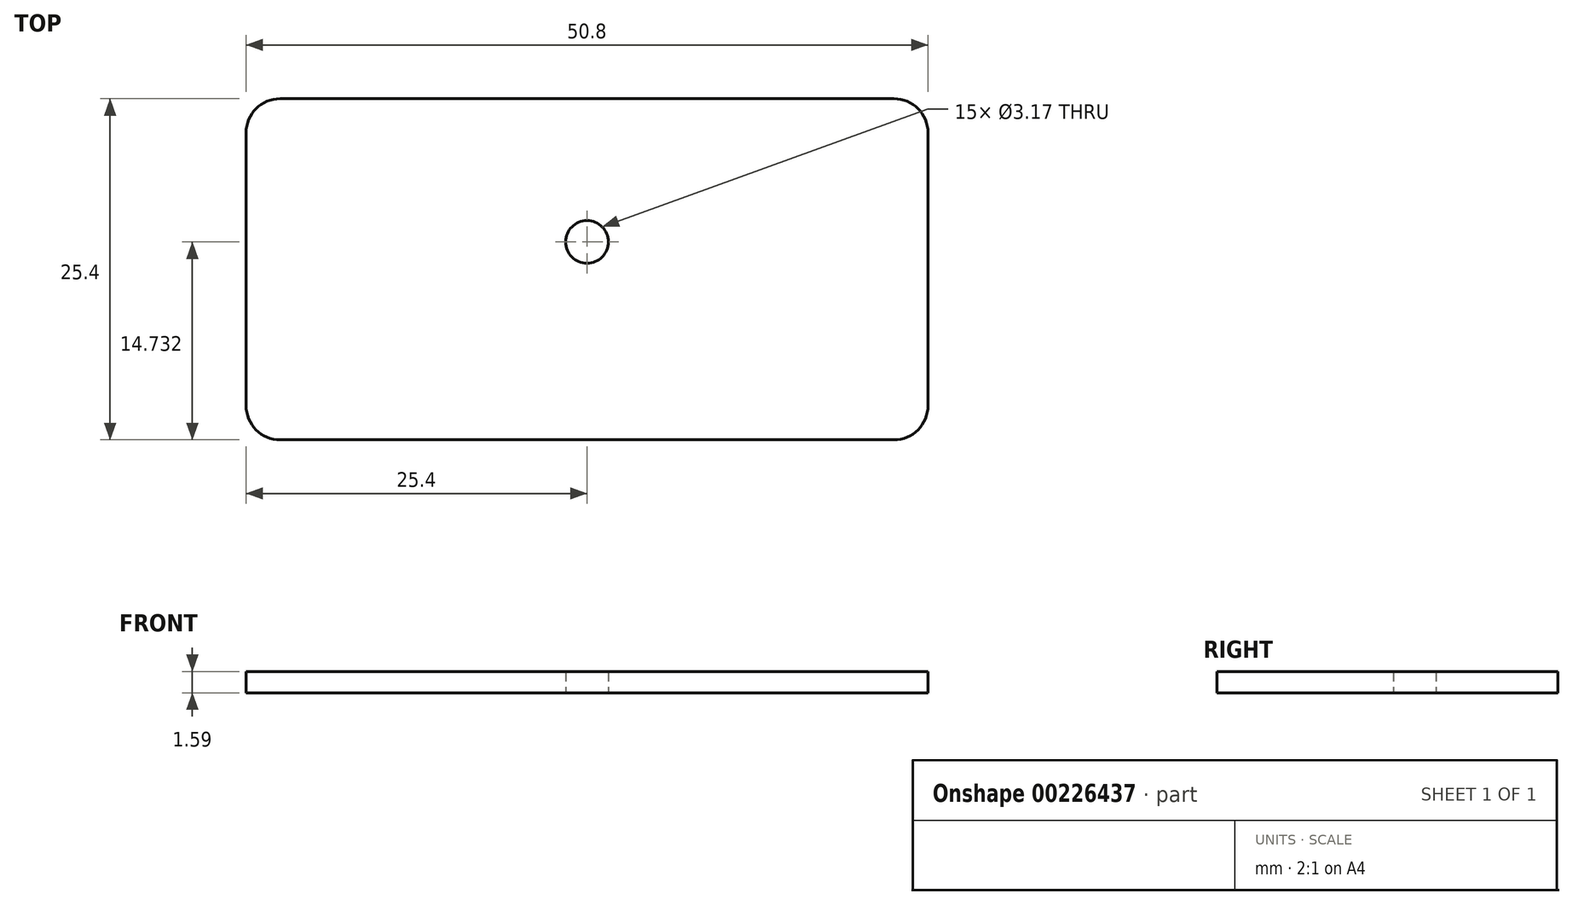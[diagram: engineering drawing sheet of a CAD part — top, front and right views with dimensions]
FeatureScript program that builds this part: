
annotation { "Feature Type Name" : "Feature", "Feature Type Description" : "" }
export const myFeature = defineFeature(function(context is Context, id is Id, definition is map)
    precondition{}
    {
        {
            var Q0;
            Q0=qCreatedBy(makeId("Top.planeOp"),FACE);
            var sketch = newSketch(context, id + "F0", { "sketchPlane" : qUnion([Q0])});
            skLineSegment(sketch, "E0.bottom", {"start": v(22.86, 12.7) * mm, "end": v(-22.86, 12.7) * mm});
            skLineSegment(sketch, "E0.top", {"start": v(22.86, -12.7) * mm, "end": v(-22.86, -12.7) * mm});
            skLineSegment(sketch, "E0.left", {"start": v(25.4, 10.16) * mm, "end": v(25.4, -10.16) * mm});
            skLineSegment(sketch, "E0.right", {"start": v(-25.4, 10.16) * mm, "end": v(-25.4, -10.16) * mm});
            skPoint(sketch, "E0.middle", {"position": v(0, 0) * mm});
            skPoint(sketch, "E1.visualSharp", {"position": v(25.4, 12.7) * mm});
            skArc(sketch, "E1.filletArc", {"start": v(25.4, 10.16) * mm, "mid": v(24.66, 11.96) * mm, "end": v(22.86, 12.7) * mm});
            skPoint(sketch, "E2.visualSharp", {"position": v(25.4, -12.7) * mm});
            skArc(sketch, "E2.filletArc", {"start": v(22.86, -12.7) * mm, "mid": v(24.66, -11.96) * mm, "end": v(25.4, -10.16) * mm});
            skPoint(sketch, "E3.visualSharp", {"position": v(-25.4, -12.7) * mm});
            skArc(sketch, "E3.filletArc", {"start": v(-25.4, -10.16) * mm, "mid": v(-24.66, -11.96) * mm, "end": v(-22.86, -12.7) * mm});
            skPoint(sketch, "E4.visualSharp", {"position": v(-25.4, 12.7) * mm});
            skArc(sketch, "E4.filletArc", {"start": v(-22.86, 12.7) * mm, "mid": v(-24.66, 11.96) * mm, "end": v(-25.4, 10.16) * mm});
            skCircle(sketch, "E5", {"center": v(0, 2.03) * mm, "radius": 1.59 * mm});
            skSolve(sketch);
        }
        {
            var Q0;
            Q0 = qSketchRegion(id + "F0", true);
            extrude(context, id + "F1", {"entities" : qUnion([Q0]), "depth" : 1.59 * mm});
        }
    });
